# Revit family: EVF-1151S
name_source: partatom
category: Communication Devices
revit_build: Autodesk Revit 2017 (Build: 20160225_1515(x64)
units: mm (PartAtom-declared; Revit-internal decimal feet)

## family parameters
Always vertical = Yes
Cut with Voids When Loaded = No
Maintain Annotation Orientation = Yes
OmniClass Number = 23.85.10.11.11.21
OmniClass Title = Speakers
Part Type = Normal
Room Calculation Point = No
Round Connector Dimension = Use Diameter
Shared = No
Work Plane-Based = Yes

## types (6) — shared parameters
ArchitectsAndEngineersSpecs = https://www.electrovoice.com
BackLength = 228.6 mm  [stored 0.75 ft]
Depth = 466.57 mm  [stored 1.53074 ft]
Description = EVS15SB 381mm LF Transducer. 103 dB Sensitivity, 135 dB Maximum SPL. System Rating: 400W Continuous, (1600W Peak). (22) M10 Threaded Suspension Points
Disclaimer = http://resource.boschsecurity.com
FrontLength = 469.84 mm
Height = 768.55 mm
IfcExportAs = IfcBuildingElementProxy
IfcExportType = IfcBuildingElementProxyType
InstallationManual = https://www.electrovoice.com
Manufacturer = Electro Voice
ManufacturerURL = https://www.electrovoice.com
PlanningTools = https://www.electrovoice.com
ProductInformation = https://www.electrovoice.com
Uniclass2015Code = Pr_60_75_08_02
Version = 1
zero-valued in all types: Default Elevation

## per-type parameters (varying)
| type | CTN | MaterialRALColour | ModelNumber |
| EVF1151SBLB_Black_1X15_Subwoofer_System | EVF1151SBLB | RAL9004 | F.01U.272.550 |
| EVF-1151S-FGB | EVF-1151S-FGB | RAL9004 | F.01U.139.625 |
| EVF-1151S-FGW | EVF-1151S-FGW | RAL9010 | F.01U.139.626 |
| EVF1151SPBLB_Black_Weatherized_1X15_Sub | EVF1151SPBLB | RAL9004 | F.01U.272.552 |
| EVF1151SPWLB_White_Weatherized_1X15_Sub | EVF1151SPWLB | RAL9010 | F.01U.272.553 |
| EVF1151SWLB_White_1X15_Subwoofer_System | EVF1151SWLB | RAL9010 | F.01U.272.551 |

note: [stored X ft] marks values corroborated as IEEE doubles in the binary element streams (Revit-internal decimal feet)

## geometry (parser evidence)
native form markers: Blend x4, Sweep x5
no freeform markers — native parametric forms only
